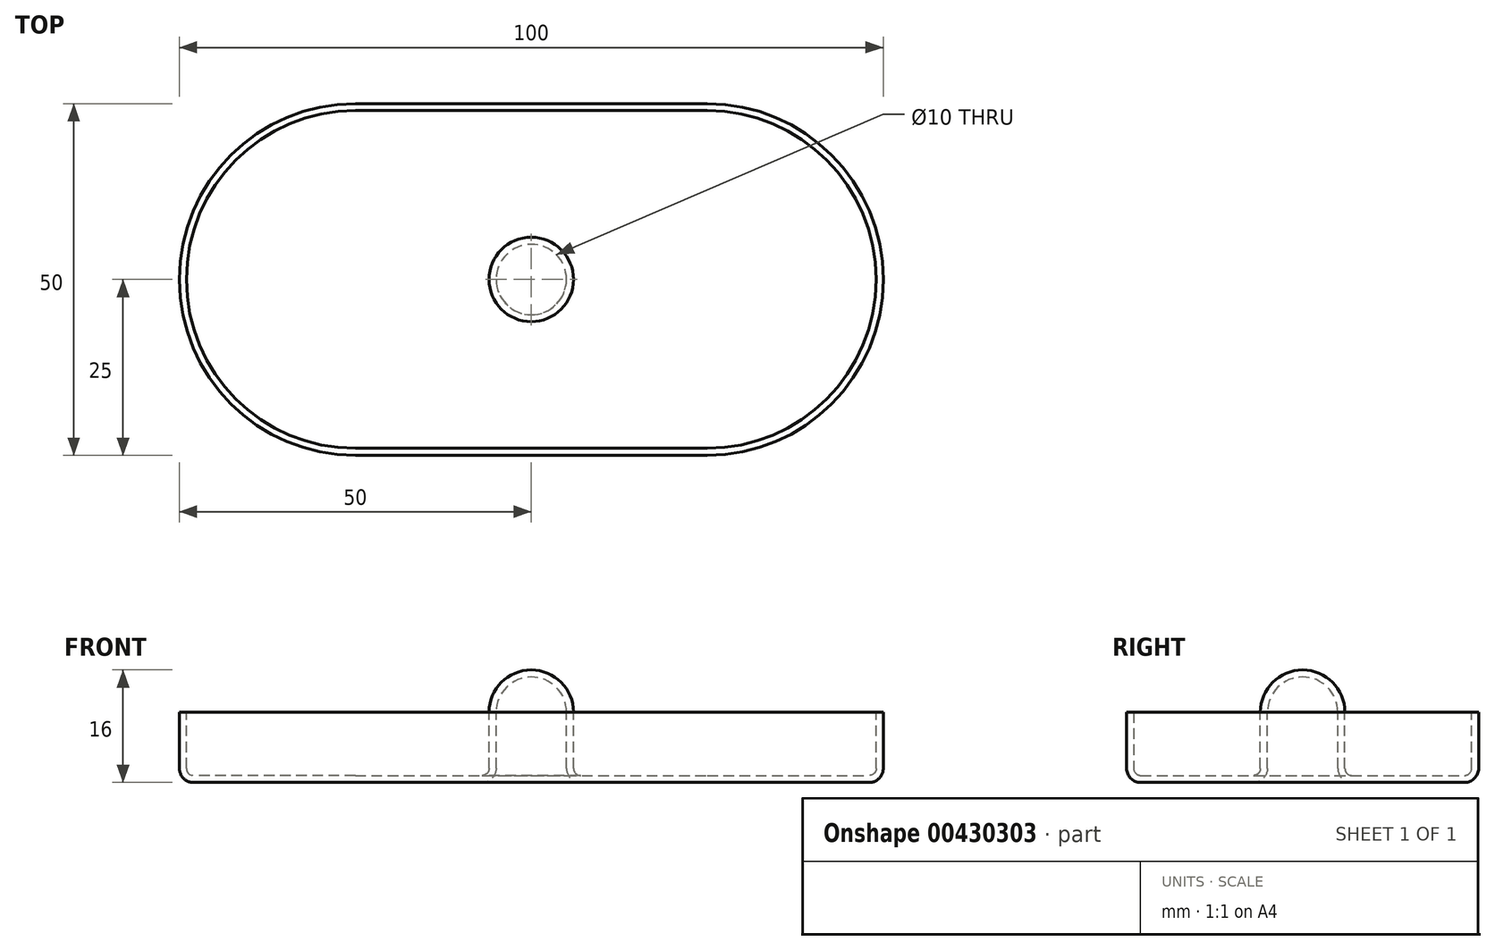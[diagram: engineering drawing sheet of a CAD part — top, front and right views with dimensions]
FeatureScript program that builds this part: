
annotation { "Feature Type Name" : "Feature", "Feature Type Description" : "" }
export const myFeature = defineFeature(function(context is Context, id is Id, definition is map)
    precondition{}
    {
        {
            var Q0;
            Q0=qCreatedBy(makeId("Top.planeOp"),FACE);
            var sketch = newSketch(context, id + "F0", { "sketchPlane" : qUnion([Q0])});
            skLineSegment(sketch, "E0.bottom", {"start": v(-50, 50) * mm, "end": v(0, 50) * mm});
            skLineSegment(sketch, "E0.top", {"start": v(-50, 0) * mm, "end": v(0, 0) * mm});
            skLineSegment(sketch, "E0.left", {"start": v(-50, 50) * mm, "end": v(-50, 0) * mm, "construction": true});
            skLineSegment(sketch, "E0.right", {"start": v(0, 50) * mm, "end": v(0, 0) * mm, "construction": true});
            skArc(sketch, "E1", {"start": v(0, 0) * mm, "mid": v(25, 25) * mm, "end": v(0, 50) * mm});
            skArc(sketch, "E2", {"start": v(-50, 50) * mm, "mid": v(-75, 25) * mm, "end": v(-50, 0) * mm});
            skLineSegment(sketch, "E3", {"start": v(-75, 25) * mm, "end": v(25, 25) * mm});
            skCircle(sketch, "E4", {"center": v(-25, 25) * mm, "radius": 5 * mm});
            skSolve(sketch);
        }
        {
            var Q0;
            {var subQ0=sQuery(id+"F0.wireOp",EDGE,"E0.top");Q0=makeQuery(id+"F0.imprint","IMPRINT",FACE,{"disambiguationData":[TD([[makeQuery(id+"F0.imprint","IMPRINT",EDGE,{"derivedFrom":subQ0}),1.0]])]});}
            var Q1;
            Q1=sQuery(id+"F0.wireOp",EDGE,"E3");
            revolve(context, id + "F1", {"entities" : qUnion([Q0]), "axis" : qUnion([Q1]), "revolveType" : RevolveType.SYMMETRIC, "angle" : 180 * degree});
        }
        {
            var Q0;
            Q0=makeQuery(id+"F1.opRevolve","CAP_FACE",FACE,{"disambiguationData":[OSD([sQuery(id+"F0.wireOp",EDGE,"E0.top"),sQuery(id+"F0.wireOp",EDGE,"E1"),sQuery(id+"F0.wireOp",EDGE,"E2"),sQuery(id+"F0.wireOp",EDGE,"E3"),sQuery(id+"F0.wireOp",EDGE,"E4")])],"isStart":true});
            var Q1;
            Q1=sQuery(id+"F0.wireOp",EDGE,"E4");
            extrude(context, id + "F2", {"entities" : qUnion([Q0]), "operationType" : NewBodyOperationType.ADD, "surfaceEntities" : qUnion([Q1]), "depth" : 10 * mm});
        }
        {
            var Q0;
            {var subQ0=sQuery(id+"F0.wireOp",EDGE,"E0.top");Q0=makeQuery(id+"F2.opExtrude","CAP_EDGE",EDGE,{"disambiguationData":[OSD([subQ0]),TDD([makeQuery(id+"F1.opRevolve","CAP_EDGE",EDGE,{"disambiguationData":[OSD([subQ0])],"isStart":true})])],"isStart":false});}
            var Q1;
            Q1=makeQuery(id+"F2.opExtrude","CAP_EDGE",EDGE,{"disambiguationData":[OSD([sQuery(id+"F0.wireOp",EDGE,"E4")])],"isStart":false});
            fillet(context, id + "F3", {"entities" : qUnion([Q0, Q1]), "radius" : 2 * mm, "tangentPropagation" : true, "allowEdgeOverflow" : false});
        }
        {
            var Q0;
            Q0=makeQuery(id+"F1.opRevolve","SWEPT_FACE",FACE,{"disambiguationData":[OSD([sQuery(id+"F0.wireOp",EDGE,"E0.top")])]});
            var Q1;
            Q1=makeQuery(id+"F1.opRevolve","SWEPT_FACE",FACE,{"disambiguationData":[OSD([sQuery(id+"F0.wireOp",EDGE,"E1")])]});
            var Q2;
            Q2=makeQuery(id+"F1.opRevolve","SWEPT_FACE",FACE,{"disambiguationData":[OSD([sQuery(id+"F0.wireOp",EDGE,"E2")])]});
            shell(context, id + "F4", {"entities" : qUnion([Q0, Q1, Q2]), "thickness" : 1 * mm});
        }
        {
            var Q0;
            Q0=makeQuery(id+"F1.opRevolve","SWEPT_BODY",BODY,{"disambiguationData":[OSD([sQuery(id+"F0.wireOp",EDGE,"E0.top"),sQuery(id+"F0.wireOp",EDGE,"E1"),sQuery(id+"F0.wireOp",EDGE,"E2"),sQuery(id+"F0.wireOp",EDGE,"E3"),sQuery(id+"F0.wireOp",EDGE,"E4")])]});
            transform(context, id + "F5", {"entities" : qUnion([Q0]), "transformType" : TransformType.TRANSLATION_3D, "dx" : 56.8 * mm, "dy" : 0 * mm, "dz" : 0 * mm, "makeCopy" : false});
        }
        {
            var Q0;
            Q0=makeQuery(id+"F1.opRevolve","SWEPT_BODY",BODY,{"disambiguationData":[OSD([sQuery(id+"F0.wireOp",EDGE,"E0.top"),sQuery(id+"F0.wireOp",EDGE,"E1"),sQuery(id+"F0.wireOp",EDGE,"E2"),sQuery(id+"F0.wireOp",EDGE,"E3"),sQuery(id+"F0.wireOp",EDGE,"E4")])]});
            var Q1;
            {var subQ0=sQuery(id+"F0.wireOp",EDGE,"E0.top");var subQ1=makeQuery(id+"F1.opRevolve","CAP_EDGE",EDGE,{"disambiguationData":[OSD([subQ0])],"isStart":false});Q1=makeQuery(id+"F4.opShell","OFFSET_EDGE",EDGE,{"disambiguationData":[OSD([subQ0]),TDD([makeQuery(id+"F3.opFillet","BLEND_EDGE",EDGE,{"blendedFrom":[makeQuery(id+"F2.opExtrude","CAP_EDGE",EDGE,{"disambiguationData":[OSD([subQ0]),TDD([subQ1])],"isStart":false}),makeQuery(id+"F2.opExtrude","SWEPT_FACE",FACE,{"disambiguationData":[OSD([subQ0]),TDD([subQ1])]})],"blendedInto":[makeQuery(id+"F2.opExtrude","SWEPT_FACE",FACE,{"disambiguationData":[OSD([subQ0]),TDD([subQ1])]})]})])]});}
            transform(context, id + "F6", {"entities" : qUnion([Q0]), "transformType" : TransformType.ROTATION, "transformAxis" : qUnion([Q1]), "angle" : 270 * degree, "makeCopy" : false});
        }
        {
            var Q0;
            {var subQ0=sQuery(id+"F0.wireOp",EDGE,"E0.top");var subQ1=makeQuery(id+"F1.opRevolve","CAP_EDGE",EDGE,{"disambiguationData":[OSD([subQ0])],"isStart":false});Q0=makeQuery(id+"F2.boolean.opBoolean","MERGE",EDGE,{"derivedFrom":[subQ1,makeQuery(id+"F2.opExtrude","CAP_EDGE",EDGE,{"disambiguationData":[OSD([subQ0]),TDD([subQ1])],"isStart":true})]});}
            cPoint(context, id + "F7", {"entities" : qUnion([Q0]), "parameter" : 0.5});
        }
        {
            var Q0;
            Q0=makeQuery(id+"F1.opRevolve","SWEPT_BODY",BODY,{"disambiguationData":[OSD([sQuery(id+"F0.wireOp",EDGE,"E0.top"),sQuery(id+"F0.wireOp",EDGE,"E1"),sQuery(id+"F0.wireOp",EDGE,"E2"),sQuery(id+"F0.wireOp",EDGE,"E3"),sQuery(id+"F0.wireOp",EDGE,"E4")])]});
            var Q1;
            Q1 = qCreatedBy(id + "F7" ,VERTEX);
            var Q2;
            Q2=qCreatedBy(makeId("Origin.pointOp"),VERTEX);
            transform(context, id + "F8", {"entities" : qUnion([Q0]), "transformType" : TransformType.TRANSLATION_ENTITY, "oppositeDirectionEntity" : false, "transformLine" : qUnion([Q1, Q2]), "makeCopy" : false});
        }
    });
